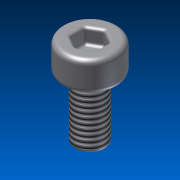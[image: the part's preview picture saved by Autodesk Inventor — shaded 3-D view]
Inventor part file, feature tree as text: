
AUTODESK INVENTOR PART (.ipt)
format: ipt  version: 2013 (Build 170138000, 138)  size: 168,960 bytes
history: native  units: mm
features: extrude x3, sketch x3, fillet x2, other x1, thread x1
ambient origin geometry x1: Origin
feature tree (10):
  other  "ソリッド1"
  extrude  "押し出し1"  Depth=5.5mm
  extrude  "押し出し2"  Depth=3.0mm TaperAngle=0.0deg
  extrude  "押し出し3"  Depth=3.0mm
  fillet  "フィレット1"  Radius=6.0mm
  fillet  "フィレット2"  Radius=1.25mm
  thread  "ねじ2"
  sketch  "スケッチ1"
  sketch  "スケッチ2"
  sketch  "スケッチ3"
